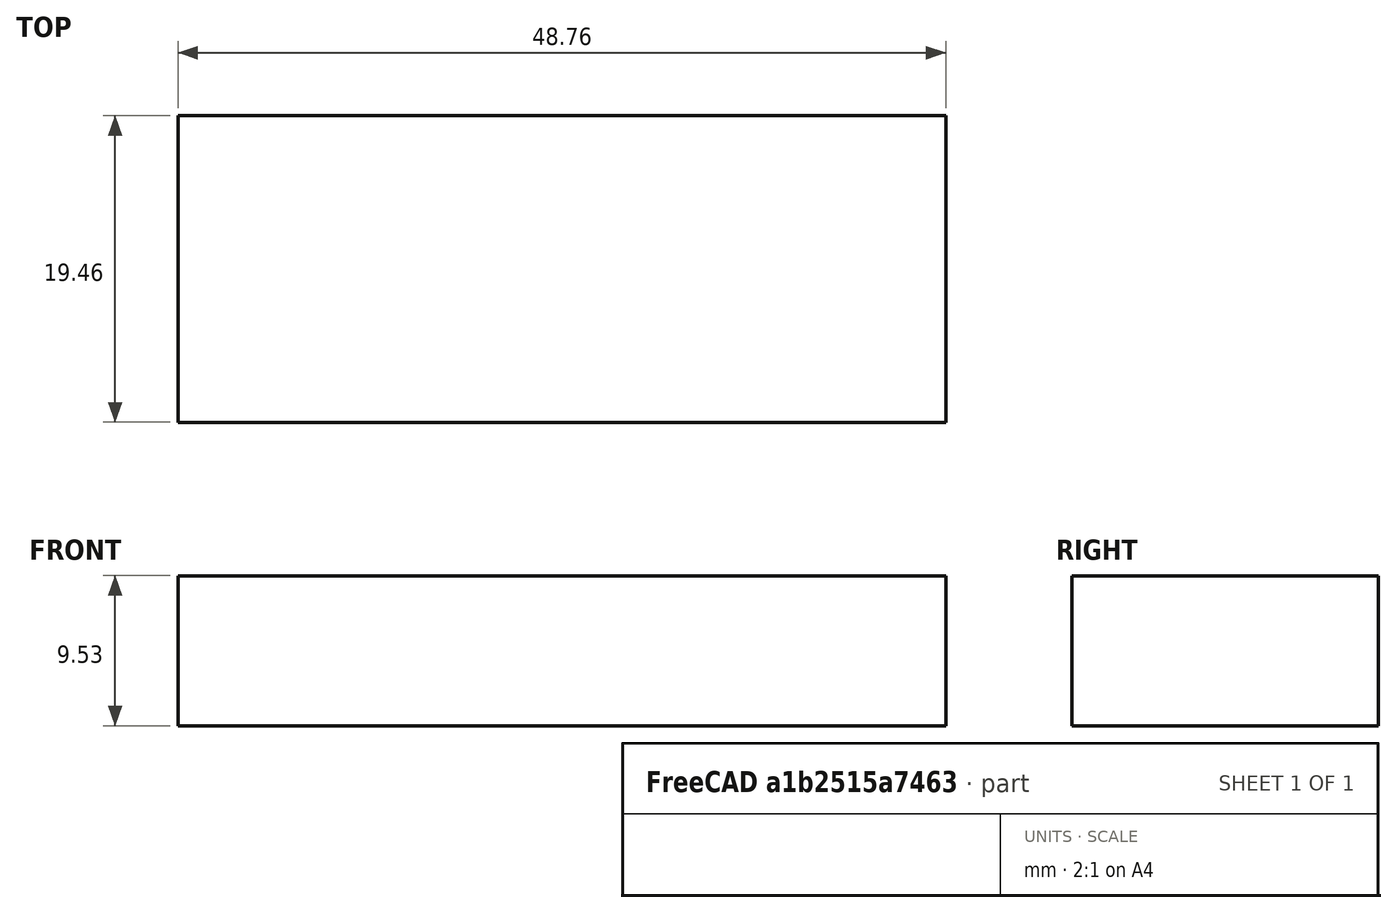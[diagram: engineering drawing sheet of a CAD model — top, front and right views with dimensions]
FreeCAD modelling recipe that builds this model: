
FCSTD DOCUMENT  (FreeCAD 0.15R4671 (Git))
Label: rx
License: All rights reserved
LicenseURL: http://en.wikipedia.org/wiki/All_rights_reserved
objects: Sketcher::SketchObject×1, PartDesign::Pad×1
note: 3 computed .brp shape members not serialized (recipe doc carries the construction recipe); baked Part::Feature solids carry a one-line shape summary decoded from their .brp

FEATURE [Sketcher::SketchObject] Sketch
  sketch-geometry (4):
    g0: LineSegment StartX=-24.384 StartY=9.73455 StartZ=0 EndX=24.384 EndY=9.73455 EndZ=0
    g1: LineSegment StartX=24.384 StartY=9.73455 StartZ=0 EndX=24.384 EndY=-9.73455 EndZ=0
    g2: LineSegment StartX=24.384 StartY=-9.73455 StartZ=0 EndX=-24.384 EndY=-9.73455 EndZ=0
    g3: LineSegment StartX=-24.384 StartY=-9.73455 StartZ=0 EndX=-24.384 EndY=9.73455 EndZ=0
  constraints (11):
    c: Coincident(g0,g1)
    c: Coincident(g1,g2)
    c: Coincident(g2,g3)
    c: Coincident(g3,g0)
    c: Horizontal(g0)
    c: Horizontal(g2)
    c: Vertical(g1)
    c: Vertical(g3)
    c: DistanceY(g1) = -19.4691
    c: DistanceX(g0) = 48.768
    c: Symmetric(g0,g1,g-1)
FEATURE [PartDesign::Pad] Pad
  Length = 9.525
  Length2 = 100
  Sketch = -> Sketch
  Type = 0
